# Revit family: Контроллер универсальный PERCo_CTL04, CTL14
name_source: partatom
category: Охранная сигнализация
units: mm (PartAtom-declared; Revit-internal decimal feet)

## family parameters
Общий = Нет
Основа = Грань
При загрузке вырезать с полостями = Нет
Размер круглого соединителя = Использовать диаметр
Сохранять ориентацию аннотаций = Да
Тип детали = Нормальный
Точка расчета площади = Нет

## types (2) — shared parameters
ADSK_URL страницы изделия = https://www.perco.ru
ADSK_Единица измерения = шт.
ADSK_Завод-изготовитель = PERCo
ADSK_Количество = 1
ADSK_Масса_Текст = не более 1,8 кг
ADSK_Материал наименование = Корпус из стали, покрытой порошковой краской
ADSK_Напряжение = 12 В
ADSK_Номинальная мощность = 3 В·А
ADSK_Ток = 0 А
Кол-во контроллеров 2-го уровня = 8
Кол-во подключаемых замков = 4
Кол-во пользователей = до 50 000
Наличие встроенного считывателя = Не предусмотрено
Наличие сканера отпечатка пальцев = нет
Отметка по умолчанию = 1500 мм
Подключение к электросети = 220В
Степень защиты оболочки = IP20
Температура использования = от +1°С до +40°С
Тип интерфейса = Ethernet
Формат читаемых карт = нет

## per-type parameters (varying)
| type | ADSK_Наименование | ADSK_Наименование краткое | CT/L04 | CT/L14 | Габаритные размеры | Кол-во выносных считывателей | Кол-во подключаемых турникетов | Кол-во событий | высота | ширина |
| CT/L04 | Контроллер универсальный замка/турникета PERCo-CT/L04.2 | Контроллер CT/L04.2 | Да | Нет | 205×189×45 мм | 4 | 1 | до 870 000 | 205 мм | 189 мм |
| CT/L14 | Контроллер универсальный замка/турникета PERCo-CT/L14 | Контроллер CT/L14 | Нет | Да | 235x208×45 мм | 8 | 2 | до 150 000 | 235 мм | 208 мм |
